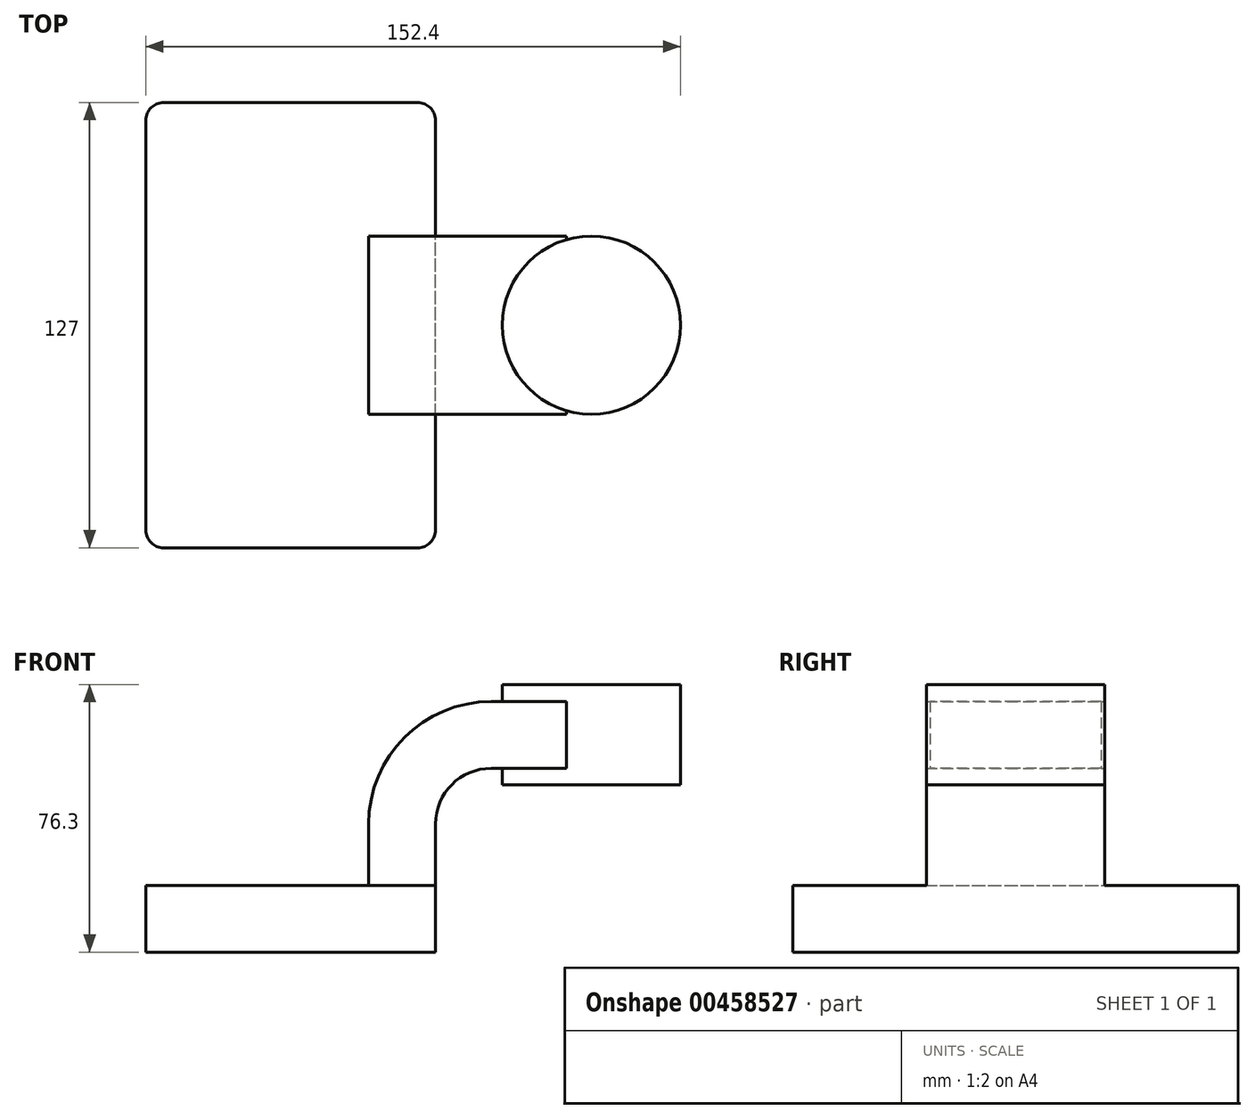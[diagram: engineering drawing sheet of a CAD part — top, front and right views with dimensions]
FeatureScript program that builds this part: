
annotation { "Feature Type Name" : "Feature", "Feature Type Description" : "" }
export const myFeature = defineFeature(function(context is Context, id is Id, definition is map)
    precondition{}
    {
        {
            var Q0;
            Q0=qCreatedBy(makeId("Front.planeOp"),FACE);
            var sketch = newSketch(context, id + "F0", { "sketchPlane" : qUnion([Q0])});
            skLineSegment(sketch, "E0.bottom", {"start": v(41.28, -9.52) * mm, "end": v(-41.28, -9.53) * mm});
            skLineSegment(sketch, "E0.top", {"start": v(41.28, 9.53) * mm, "end": v(-41.28, 9.52) * mm});
            skLineSegment(sketch, "E0.left", {"start": v(41.28, -9.52) * mm, "end": v(41.28, 9.53) * mm});
            skLineSegment(sketch, "E0.right", {"start": v(-41.28, -9.53) * mm, "end": v(-41.28, 9.52) * mm});
            skPoint(sketch, "E0.middle", {"position": v(0, 0) * mm});
            skLineSegment(sketch, "E1.bottom", {"start": v(111.12, 38.2) * mm, "end": v(60.32, 38.2) * mm});
            skLineSegment(sketch, "E1.top", {"start": v(111.12, 66.77) * mm, "end": v(60.32, 66.77) * mm});
            skLineSegment(sketch, "E1.left", {"start": v(111.12, 38.2) * mm, "end": v(111.12, 66.77) * mm});
            skLineSegment(sketch, "E1.right", {"start": v(60.32, 38.2) * mm, "end": v(60.32, 66.77) * mm});
            skPoint(sketch, "E1.middle", {"position": v(85.72, 52.48) * mm});
            skLineSegment(sketch, "E2", {"start": v(41.28, 9.53) * mm, "end": v(41.28, 27) * mm});
            skArc(sketch, "E3", {"start": v(41.28, 27) * mm, "mid": v(45.92, 38.23) * mm, "end": v(57.15, 42.88) * mm});
            skLineSegment(sketch, "E4", {"start": v(57.15, 42.88) * mm, "end": v(78.64, 42.88) * mm});
            skLineSegment(sketch, "E5.0", {"start": v(57.15, 61.93) * mm, "end": v(78.64, 61.93) * mm});
            skArc(sketch, "E5.1", {"start": v(22.23, 27) * mm, "mid": v(32.45, 51.7) * mm, "end": v(57.15, 61.93) * mm});
            skLineSegment(sketch, "E5.2", {"start": v(22.23, 9.53) * mm, "end": v(22.23, 27) * mm});
            skFitSpline(sketch, "E6", {"points": [v(-41.28, 9.52) * mm, v(57.15, 61.93) * mm], "startDerivative": vector(24.09, 109.75) * mm, "endDerivative": vector(142.38, -5.74) * mm});
            skLineSegment(sketch, "E7", {"start": v(85.72, 38.2) * mm, "end": v(85.72, 66.77) * mm});
            skLineSegment(sketch, "E8", {"start": v(78.64, 42.88) * mm, "end": v(78.64, 61.93) * mm});
            skSolve(sketch);
        }
        {
            var Q0;
            Q0 = qSketchRegion(id + "Fy6y5D2GCniz7Gm_0", true);
            var Q1;
            Q1=makeQuery(id+"F0.imprint","IMPRINT",FACE,{"disambiguationData":[TD([[makeQuery(id+"F0.imprint","IMPRINT",EDGE,{"derivedFrom":sQuery(id+"F0.wireOp",EDGE,"E0.bottom")}),-1.0]])]});
            extrude(context, id + "F1", {"entities" : qUnion([Q0, Q1]), "endBound" : BoundingType.SYMMETRIC, "depth" : 127 * mm});
        }
        {
            var Q0;
            {var subQ1=sQuery(id+"F0.wireOp",EDGE,"E2");Q0=makeQuery(id+"F0.imprint","IMPRINT",FACE,{"disambiguationData":[TD([[makeQuery(id+"F0.imprint","IMPRINT",EDGE,{"derivedFrom":subQ1}),1.0]])]});}
            var Q1;
            {var subQ5=sQuery(id+"F0.wireOp",EDGE,"E8");Q1=makeQuery(id+"F0.imprint","IMPRINT",FACE,{"disambiguationData":[TD([[makeQuery(id+"F0.imprint","IMPRINT",EDGE,{"derivedFrom":subQ5}),1.0]])]});}
            extrude(context, id + "F2", {"entities" : qUnion([Q0, Q1]), "operationType" : NewBodyOperationType.ADD, "endBound" : BoundingType.SYMMETRIC, "depth" : 50.8 * mm});
        }
        {
            var Q0;
            Q0=makeQuery(id+"F0.imprint","IMPRINT",FACE,{"disambiguationData":[TD([[makeQuery(id+"F0.imprint","IMPRINT",EDGE,{"derivedFrom":sQuery(id+"F0.wireOp",EDGE,"E5.1")}),1.0]])]});
            extrude(context, id + "F3", {"entities" : qUnion([Q0]), "operationType" : NewBodyOperationType.ADD, "endBound" : BoundingType.SYMMETRIC, "depth" : 15.88 * mm});
        }
        {
            var Q0;
            {var subQ0=sQuery(id+"F0.wireOp",EDGE,"E1.left");Q0=makeQuery(id+"F0.imprint","IMPRINT",FACE,{"disambiguationData":[TD([[makeQuery(id+"F0.imprint","IMPRINT",EDGE,{"derivedFrom":subQ0}),1.0]])]});}
            var Q1;
            Q1=sQuery(id+"F0.wireOp",EDGE,"E7");
            revolve(context, id + "F4", {"operationType" : NewBodyOperationType.ADD, "entities" : qUnion([Q0]), "axis" : qUnion([Q1]), "revolveType" : RevolveType.FULL});
        }
        {
            var Q0;
            Q0=makeQuery(id+"F1.opExtrude","CAP_EDGE",EDGE,{"disambiguationData":[OSD([sQuery(id+"F0.wireOp",EDGE,"E0.left")])],"isStart":false});
            var Q1;
            Q1=makeQuery(id+"F1.opExtrude","CAP_EDGE",EDGE,{"disambiguationData":[OSD([sQuery(id+"F0.wireOp",EDGE,"E0.left")])],"isStart":true});
            var Q2;
            Q2=makeQuery(id+"F1.opExtrude","CAP_EDGE",EDGE,{"disambiguationData":[OSD([sQuery(id+"F0.wireOp",EDGE,"E0.right")])],"isStart":true});
            var Q3;
            Q3=makeQuery(id+"F1.opExtrude","CAP_EDGE",EDGE,{"disambiguationData":[OSD([sQuery(id+"F0.wireOp",EDGE,"E0.right")])],"isStart":false});
            fillet(context, id + "F5", {"entities" : qUnion([Q0, Q1, Q2, Q3]), "radius" : 5.08 * mm, "tangentPropagation" : true, "allowEdgeOverflow" : false});
        }
    });
